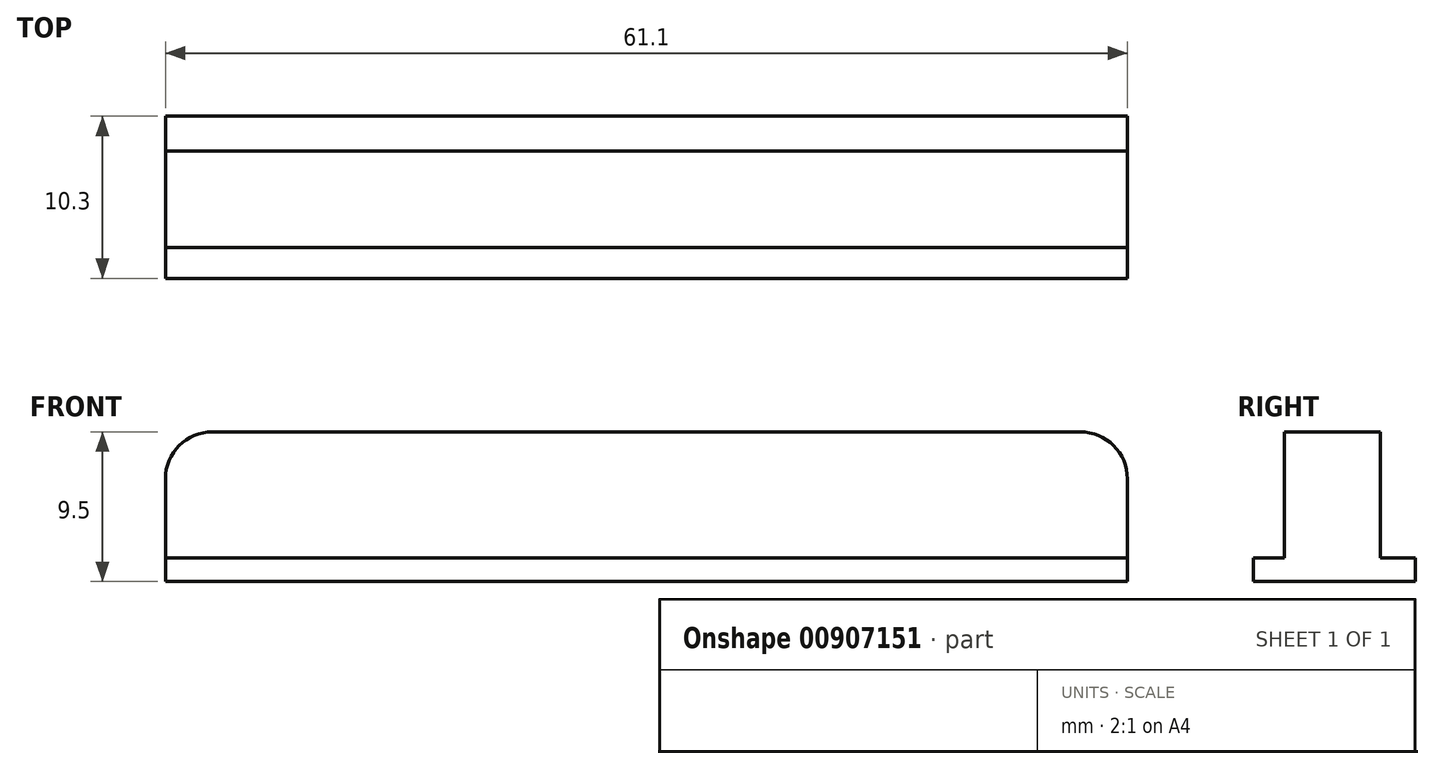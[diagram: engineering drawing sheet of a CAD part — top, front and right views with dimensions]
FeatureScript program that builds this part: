
annotation { "Feature Type Name" : "Feature", "Feature Type Description" : "" }
export const myFeature = defineFeature(function(context is Context, id is Id, definition is map)
    precondition{}
    {
        {
            var Q0;
            Q0=qCreatedBy(makeId("Front.planeOp"),FACE);
            var sketch = newSketch(context, id + "F0", { "sketchPlane" : qUnion([Q0])});
            skLineSegment(sketch, "E0.bottom", {"start": v(-30.82, 19.1) * mm, "end": v(24.28, 19.1) * mm});
            skLineSegment(sketch, "E0.top", {"start": v(-33.82, 9.6) * mm, "end": v(27.28, 9.6) * mm});
            skLineSegment(sketch, "E0.left", {"start": v(-33.82, 16.1) * mm, "end": v(-33.82, 9.6) * mm});
            skLineSegment(sketch, "E0.right", {"start": v(27.28, 16.1) * mm, "end": v(27.28, 9.6) * mm});
            skPoint(sketch, "E1.visualSharp", {"position": v(-33.82, 19.1) * mm});
            skArc(sketch, "E1.filletArc", {"start": v(-30.82, 19.1) * mm, "mid": v(-32.94, 18.21) * mm, "end": v(-33.82, 16.1) * mm});
            skPoint(sketch, "E2.visualSharp", {"position": v(27.28, 19.1) * mm});
            skArc(sketch, "E2.filletArc", {"start": v(27.28, 16.1) * mm, "mid": v(26.4, 18.21) * mm, "end": v(24.28, 19.1) * mm});
            skSolve(sketch);
        }
        {
            var Q0;
            Q0 = qSketchRegion(id + "F0", true);
            extrude(context, id + "F1", {"entities" : qUnion([Q0]), "depth" : 10.3 * mm, "offsetDistance" : 25 * mm});
        }
        {
            var Q0;
            Q0=makeQuery(id+"F1.opExtrude","SWEPT_FACE",FACE,{"disambiguationData":[OSD([sQuery(id+"F0.wireOp",EDGE,"E0.right")])]});
            var sketch = newSketch(context, id + "F2", { "sketchPlane" : qUnion([Q0])});
            skLineSegment(sketch, "E3.bottom", {"start": v(-10.4, 19.63) * mm, "end": v(-8.33, 19.63) * mm});
            skLineSegment(sketch, "E3.top", {"start": v(-10.4, 11.1) * mm, "end": v(-8.33, 11.1) * mm});
            skLineSegment(sketch, "E3.left", {"start": v(-10.4, 19.63) * mm, "end": v(-10.4, 11.1) * mm});
            skLineSegment(sketch, "E3.right", {"start": v(-8.33, 19.63) * mm, "end": v(-8.33, 11.1) * mm});
            skLineSegment(sketch, "E4.bottom", {"start": v(0, 19.82) * mm, "end": v(-2.23, 19.82) * mm});
            skLineSegment(sketch, "E4.top", {"start": v(0, 11.1) * mm, "end": v(-2.23, 11.1) * mm});
            skLineSegment(sketch, "E4.left", {"start": v(0, 19.82) * mm, "end": v(0, 11.1) * mm});
            skLineSegment(sketch, "E4.right", {"start": v(-2.23, 19.82) * mm, "end": v(-2.23, 11.1) * mm});
            skSolve(sketch);
        }
        {
            var Q0;
            Q0 = qSketchRegion(id + "F2", true);
            extrude(context, id + "F3", {"entities" : qUnion([Q0]), "operationType" : NewBodyOperationType.REMOVE, "endBound" : BoundingType.THROUGH_ALL, "oppositeDirection" : true, "depth" : 25 * mm, "offsetDistance" : 25 * mm});
        }
    });
